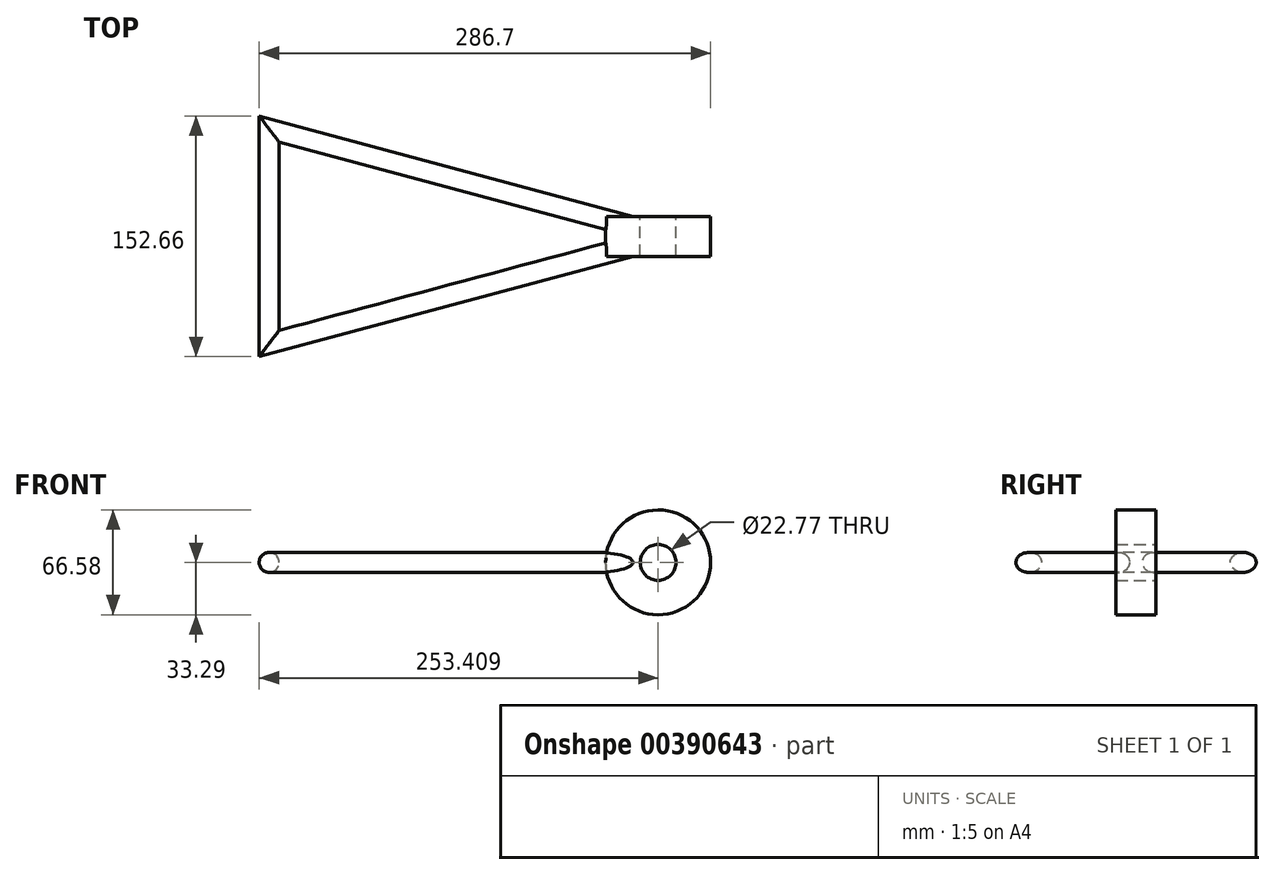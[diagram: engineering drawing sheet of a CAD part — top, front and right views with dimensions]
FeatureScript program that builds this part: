
annotation { "Feature Type Name" : "Feature", "Feature Type Description" : "" }
export const myFeature = defineFeature(function(context is Context, id is Id, definition is map)
    precondition{}
    {
        {
            var Q0;
            Q0=qCreatedBy(makeId("Top.planeOp"),FACE);
            var sketch = newSketch(context, id + "F0", { "sketchPlane" : qUnion([Q0])});
            skLineSegment(sketch, "E0", {"start": v(0, 68.06) * mm, "end": v(0, -68.06) * mm});
            skLineSegment(sketch, "E1", {"start": v(0, -68.06) * mm, "end": v(254, 0) * mm});
            skLineSegment(sketch, "E2", {"start": v(254, 0) * mm, "end": v(0, 68.06) * mm});
            skSolve(sketch);
        }
        {
            var Q0;
            Q0=qCreatedBy(makeId("Front.planeOp"),FACE);
            var sketch = newSketch(context, id + "F1", { "sketchPlane" : qUnion([Q0])});
            skCircle(sketch, "E3", {"center": v(0, 0) * mm, "radius": 6.35 * mm});
            skSolve(sketch);
        }
        {
            var Q0;
            Q0 = qSketchRegion(id + "F1", true);
            var Q1;
            Q1=sQuery(id+"F1.wireOp",EDGE,"E3");
            var Q2;
            Q2 = qConstructionFilter(qBodyType(qCreatedBy(id + "F0" ,EDGE), BodyType.WIRE), ConstructionObject.NO);
            sweep(context, id + "F2", {"profiles" : qUnion([Q0]), "surfaceProfiles" : qUnion([Q1]), "path" : qUnion([Q2])});
        }
        {
            var Q0;
            Q0=qCreatedBy(makeId("Front.planeOp"),FACE);
            var sketch = newSketch(context, id + "F3", { "sketchPlane" : qUnion([Q0])});
            skCircle(sketch, "E4", {"center": v(247.06, 0) * mm, "radius": 33.3 * mm});
            skSolve(sketch);
        }
        {
            var Q0;
            Q0 = qSketchRegion(id + "F3", true);
            extrude(context, id + "F4", {"entities" : qUnion([Q0]), "operationType" : NewBodyOperationType.ADD, "depth" : 12.7 * mm, "hasSecondDirection" : true, "secondDirectionOppositeDirection" : true, "secondDirectionDepth" : 12.7 * mm});
        }
        {
            var Q0;
            Q0=makeQuery(id+"F4.opExtrude","CAP_FACE",FACE,{"disambiguationData":[OSD([sQuery(id+"F3.wireOp",EDGE,"E4")])],"isStart":true});
            var sketch = newSketch(context, id + "F5", { "sketchPlane" : qUnion([Q0])});
            skCircle(sketch, "E5", {"center": v(-247.06, 0) * mm, "radius": 11.38 * mm});
            skSolve(sketch);
        }
        {
            var Q0;
            Q0 = qSketchRegion(id + "F5", true);
            extrude(context, id + "F6", {"entities" : qUnion([Q0]), "operationType" : NewBodyOperationType.REMOVE, "oppositeDirection" : true, "depth" : 25.4 * mm});
        }
    });
